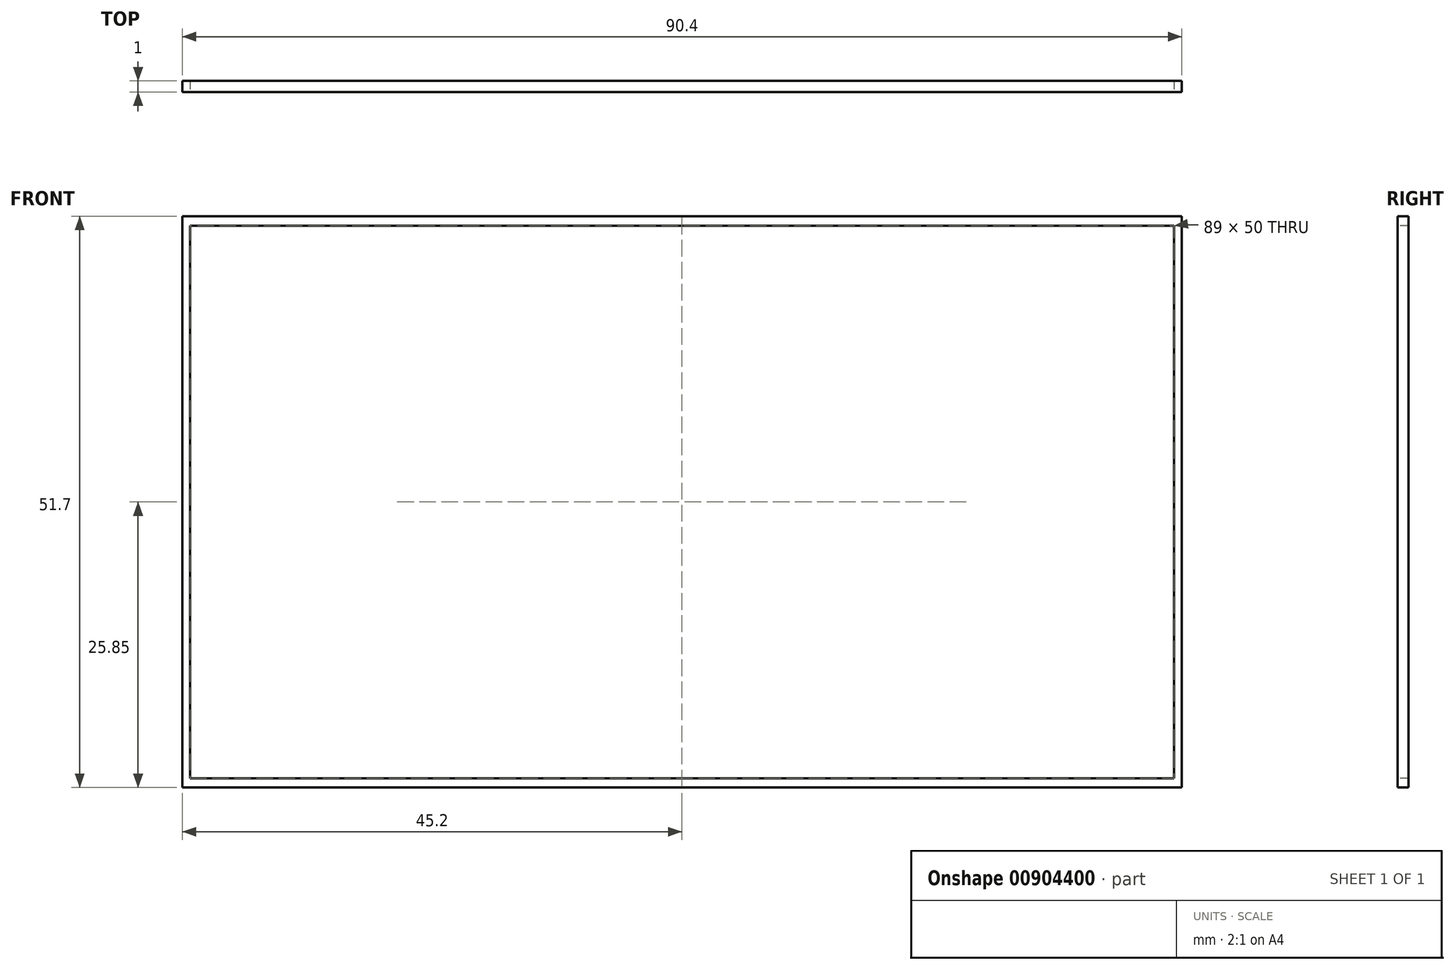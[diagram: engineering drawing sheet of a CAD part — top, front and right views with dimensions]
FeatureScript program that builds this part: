
annotation { "Feature Type Name" : "Feature", "Feature Type Description" : "" }
export const myFeature = defineFeature(function(context is Context, id is Id, definition is map)
    precondition{}
    {
        {
            var Q0;
            Q0=qCreatedBy(makeId("Front.planeOp"),FACE);
            var sketch = newSketch(context, id + "F0", { "sketchPlane" : qUnion([Q0])});
            skLineSegment(sketch, "E0.bottom", {"start": v(-45.2, 25.85) * mm, "end": v(45.2, 25.85) * mm});
            skLineSegment(sketch, "E0.top", {"start": v(-45.2, -25.85) * mm, "end": v(45.2, -25.85) * mm});
            skLineSegment(sketch, "E0.left", {"start": v(-45.2, 25.85) * mm, "end": v(-45.2, -25.85) * mm});
            skLineSegment(sketch, "E0.right", {"start": v(45.2, 25.85) * mm, "end": v(45.2, -25.85) * mm});
            skSolve(sketch);
        }
        {
            var Q0;
            Q0 = qSketchRegion(id + "F0", true);
            extrude(context, id + "F1", {"entities" : qUnion([Q0]), "oppositeDirection" : true, "depth" : 1 * mm, "offsetDistance" : 25 * mm});
        }
        {
            var Q0;
            Q0=makeQuery(id+"F1.opExtrude","CAP_FACE",FACE,{"disambiguationData":[OSD([sQuery(id+"F0.wireOp",EDGE,"E0.bottom"),sQuery(id+"F0.wireOp",EDGE,"E0.top"),sQuery(id+"F0.wireOp",EDGE,"E0.left"),sQuery(id+"F0.wireOp",EDGE,"E0.right")])],"isStart":true});
            var sketch = newSketch(context, id + "F2", { "sketchPlane" : qUnion([Q0])});
            skLineSegment(sketch, "E1.bottom", {"start": v(-44.5, 25) * mm, "end": v(44.5, 25) * mm});
            skLineSegment(sketch, "E1.top", {"start": v(-44.5, -25) * mm, "end": v(44.5, -25) * mm});
            skLineSegment(sketch, "E1.left", {"start": v(-44.5, 25) * mm, "end": v(-44.5, -25) * mm});
            skLineSegment(sketch, "E1.right", {"start": v(44.5, 25) * mm, "end": v(44.5, -25) * mm});
            skSolve(sketch);
        }
        {
            var Q0;
            Q0 = qSketchRegion(id + "F2", true);
            extrude(context, id + "F3", {"entities" : qUnion([Q0]), "operationType" : NewBodyOperationType.REMOVE, "oppositeDirection" : true, "depth" : 25 * mm, "offsetDistance" : 25 * mm});
        }
    });
